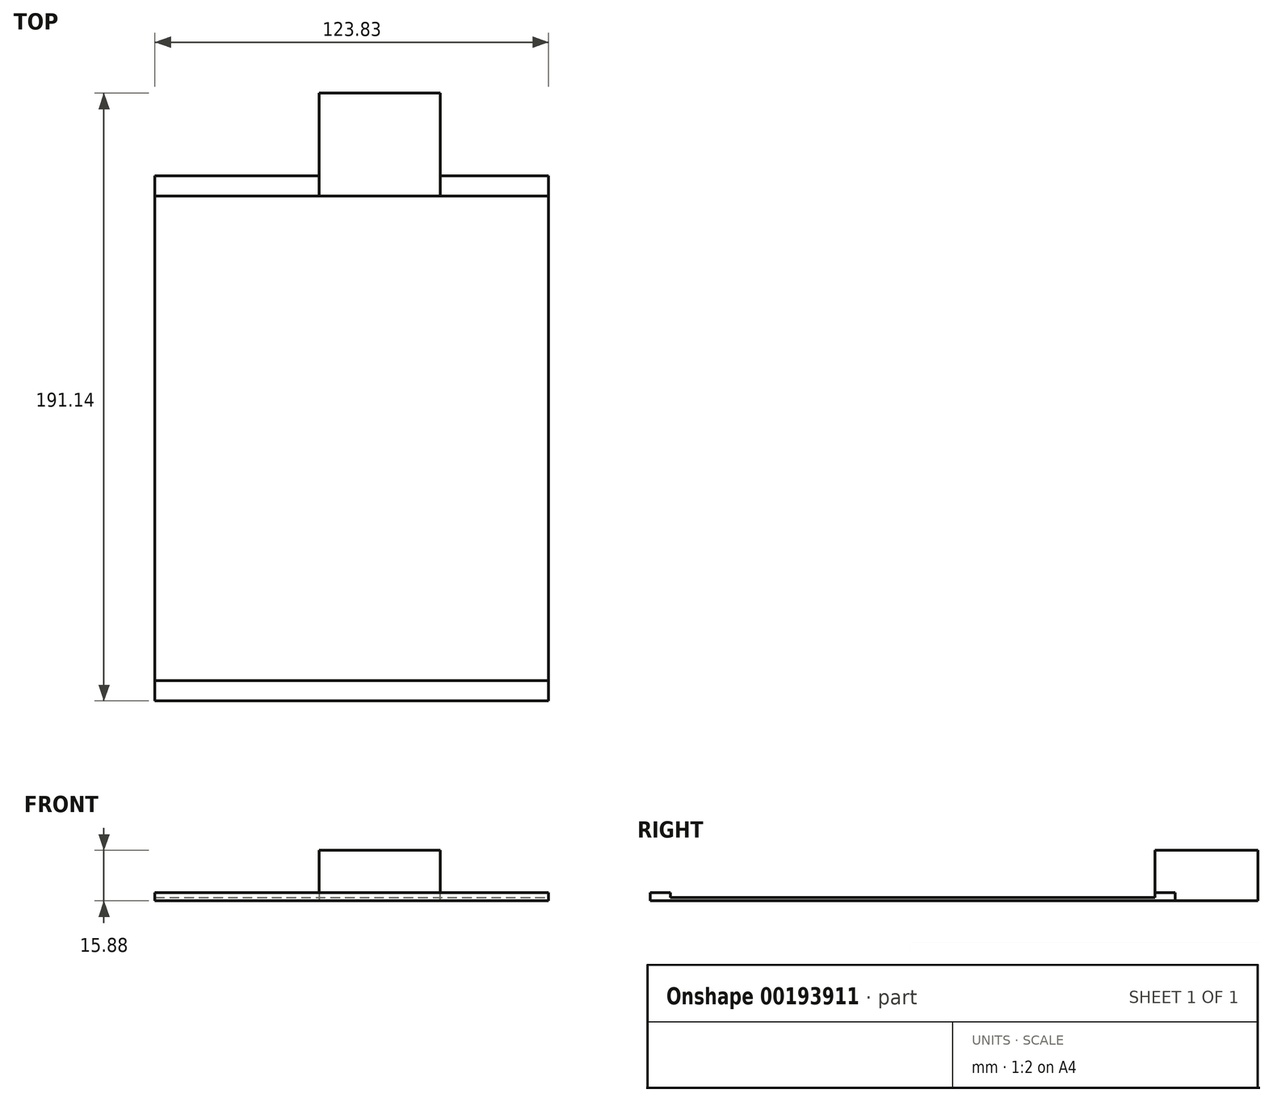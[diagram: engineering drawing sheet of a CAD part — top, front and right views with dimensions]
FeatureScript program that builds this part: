
annotation { "Feature Type Name" : "Feature", "Feature Type Description" : "" }
export const myFeature = defineFeature(function(context is Context, id is Id, definition is map)
    precondition{}
    {
        {
            var Q0;
            Q0=qCreatedBy(makeId("Top.planeOp"),FACE);
            var sketch = newSketch(context, id + "F0", { "sketchPlane" : qUnion([Q0])});
            skLineSegment(sketch, "E0.bottom", {"start": v(-64.56, 71) * mm, "end": v(59.27, 71) * mm});
            skLineSegment(sketch, "E0.top", {"start": v(-64.56, -81.4) * mm, "end": v(59.27, -81.4) * mm});
            skLineSegment(sketch, "E0.left", {"start": v(-64.56, 71) * mm, "end": v(-64.56, -81.4) * mm});
            skLineSegment(sketch, "E0.right", {"start": v(59.27, 71) * mm, "end": v(59.27, -81.4) * mm});
            skLineSegment(sketch, "E1", {"start": v(-64.56, -81.4) * mm, "end": v(-64.56, -87.75) * mm});
            skLineSegment(sketch, "E2", {"start": v(-64.56, -87.75) * mm, "end": v(59.27, -87.75) * mm});
            skLineSegment(sketch, "E3", {"start": v(59.27, -87.75) * mm, "end": v(59.27, -81.4) * mm});
            skLineSegment(sketch, "E4", {"start": v(59.27, 71) * mm, "end": v(59.27, 77.35) * mm});
            skLineSegment(sketch, "E5", {"start": v(59.27, 77.35) * mm, "end": v(-64.56, 77.35) * mm});
            skLineSegment(sketch, "E6", {"start": v(-64.56, 77.35) * mm, "end": v(-64.56, 71) * mm});
            skLineSegment(sketch, "E7", {"start": v(-12.94, 71) * mm, "end": v(-12.94, 103.4) * mm});
            skLineSegment(sketch, "E8", {"start": v(-12.94, 103.4) * mm, "end": v(25.16, 103.4) * mm});
            skLineSegment(sketch, "E9", {"start": v(25.16, 103.4) * mm, "end": v(25.16, 71) * mm});
            skSolve(sketch);
        }
        {
            var Q0;
            Q0=makeQuery(id+"F0.imprint","IMPRINT",FACE,{"disambiguationData":[TD([[makeQuery(id+"F0.imprint","IMPRINT",EDGE,{"derivedFrom":sQuery(id+"F0.wireOp",EDGE,"E0.top")}),1.0]])]});
            extrude(context, id + "F1", {"entities" : qUnion([Q0]), "depth" : (1 + (1 / 8)) * mm});
        }
        {
            var Q0;
            {var subQ0=sQuery(id+"F0.wireOp",EDGE,"E6");Q0=makeQuery(id+"F0.imprint","IMPRINT",FACE,{"disambiguationData":[TD([[makeQuery(id+"F0.imprint","IMPRINT",EDGE,{"derivedFrom":subQ0}),1.0]])]});}
            var Q1;
            {var subQ0=sQuery(id+"F0.wireOp",EDGE,"E7");var subQ1=sQuery(id+"F0.wireOp",EDGE,"E0.bottom");var subQ2=makeQuery(id+"F0.imprint","INTERSECT",VERTEX,{"derivedFrom":[subQ1,subQ0]});Q1=makeQuery(id+"F0.imprint","IMPRINT",FACE,{"disambiguationData":[TD([[makeQuery(id+"F0.imprint","IMPRINT",EDGE,{"disambiguationData":[TD([[subQ2,-1.0]])],"derivedFrom":subQ1}),1.0]])]});}
            var Q2;
            {var subQ0=sQuery(id+"F0.wireOp",EDGE,"E4");Q2=makeQuery(id+"F0.imprint","IMPRINT",FACE,{"disambiguationData":[TD([[makeQuery(id+"F0.imprint","IMPRINT",EDGE,{"derivedFrom":subQ0}),1.0]])]});}
            var Q3;
            Q3=makeQuery(id+"F0.imprint","IMPRINT",FACE,{"disambiguationData":[TD([[makeQuery(id+"F0.imprint","IMPRINT",EDGE,{"derivedFrom":sQuery(id+"F0.wireOp",EDGE,"E0.top")}),-1.0]])]});
            extrude(context, id + "F2", {"entities" : qUnion([Q0, Q1, Q2, Q3]), "operationType" : NewBodyOperationType.ADD, "depth" : 2.54 * mm});
        }
        {
            var Q0;
            {var subQ0=sQuery(id+"F0.wireOp",EDGE,"E7");var subQ1=sQuery(id+"F0.wireOp",EDGE,"E0.bottom");var subQ2=makeQuery(id+"F0.imprint","INTERSECT",VERTEX,{"derivedFrom":[subQ1,subQ0]});Q0=makeQuery(id+"F0.imprint","IMPRINT",FACE,{"disambiguationData":[TD([[makeQuery(id+"F0.imprint","IMPRINT",EDGE,{"disambiguationData":[TD([[subQ2,-1.0]])],"derivedFrom":subQ1}),1.0]])]});}
            var Q1;
            {var subQ5=sQuery(id+"F0.wireOp",EDGE,"E8");Q1=makeQuery(id+"F0.imprint","IMPRINT",FACE,{"disambiguationData":[TD([[makeQuery(id+"F0.imprint","IMPRINT",EDGE,{"derivedFrom":subQ5}),-1.0]])]});}
            extrude(context, id + "F3", {"entities" : qUnion([Q0, Q1]), "operationType" : NewBodyOperationType.ADD, "depth" : 15.88 * mm});
        }
    });
